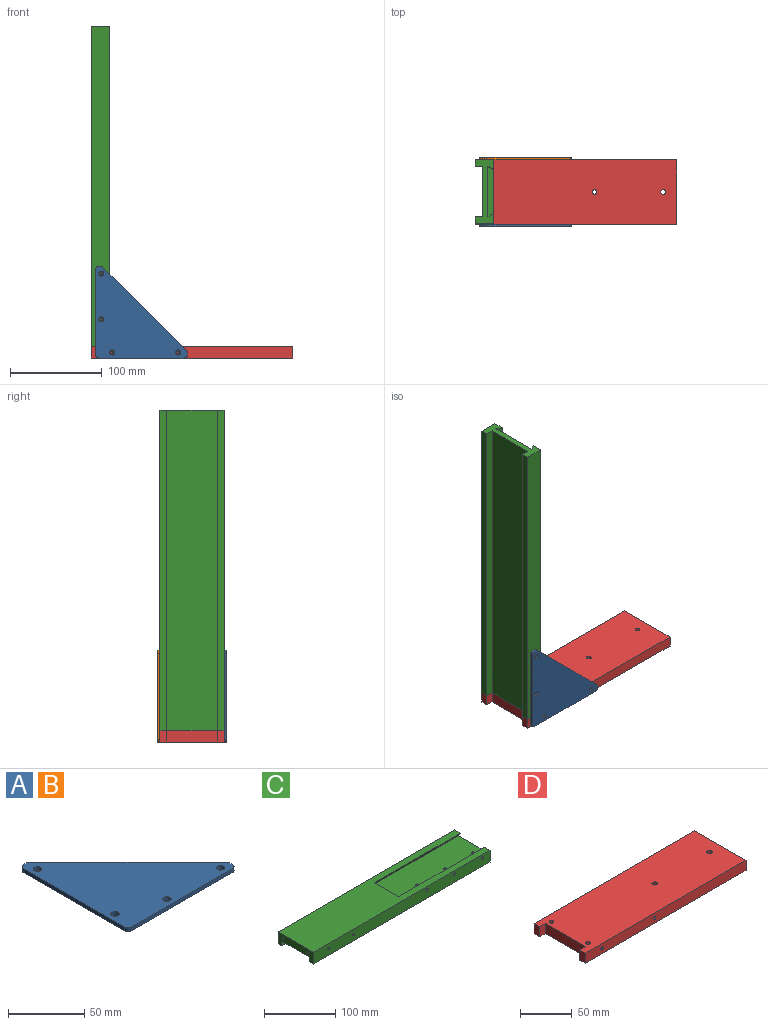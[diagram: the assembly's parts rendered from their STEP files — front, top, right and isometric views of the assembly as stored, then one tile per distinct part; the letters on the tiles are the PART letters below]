
ASSEMBLY  parts=4 mates=3
PART A: 16 faces, bbox 100x100x3 mm
  f0: plane 3x2.76mm, normal (0,1,0), area 8.3mm2, adj f1,f8,f9,f10
  f1: cylinder r=3mm len=3mm, axis (0,0,1), area 14.1mm2, adj f0,f2,f8,f9
  f2: plane 94x3mm, normal (-1,0,0), area 282mm2, adj f1,f3,f8,f9
  f3: cylinder r=3mm len=3mm, axis (0,0,1), area 14.1mm2, adj f2,f4,f8,f9
  f4: plane 94x3mm, normal (0,-1,0), area 282mm2, adj f3,f5,f8,f9
  f5: cylinder r=3mm len=3mm, axis (0,0,1), area 14.1mm2, adj f4,f6,f8,f9
  f6: plane 3x2.76mm, normal (1,0,0), area 8.3mm2, adj f5,f8,f9,f11
  f7: plane 91.24x91.24mm, normal (0.71,0.71,0), area 387.1mm2, adj f8,f9,f10,f11
  f8: plane 100x100mm, normal (0,0,1), area 5574.3mm2, adj f0,f1,f2,f3,f4,f5,f6,f7
  f9: plane 100x100mm, normal (0,0,-1), area 5574.3mm2, adj f0,f1,f2,f3,f4,f5,f6,f7
  f10: cylinder r=3mm len=3mm, axis (0,0,1), area 7.1mm2, adj f0,f7,f8,f9
  f11: cylinder r=3mm len=3mm, axis (0,0,1), area 7.1mm2, adj f6,f7,f8,f9
  f12: cylinder r=2.75mm len=5.5mm, axis (0,0,1), area 51.8mm2, adj f8,f9
  f13: cylinder r=2.75mm len=5.5mm, axis (0,0,1), area 51.8mm2, adj f8,f9
  f14: cylinder r=2.75mm len=5.5mm, axis (0,0,1), area 51.8mm2, adj f8,f9
  f15: cylinder r=2.75mm len=5.5mm, axis (0,0,1), area 51.8mm2, adj f8,f9
PART B: same geometry as A
PART C: 32 faces, bbox 350x70x20 mm
  f0: plane 170x55mm, normal (0,0,1), area 9166.6mm2, adj f2,f8,f24,f25,f26,f27,f28,f29
  f1: plane 350x7.5mm, normal (0,0,-1), area 2625mm2, adj f2,f4,f5,f9
  f2: plane 70x20mm, normal (1,0,0), area 651mm2, adj f0,f1,f3,f4,f6,f7,f9,f10
  f3: plane 350x20mm, normal (0,-1,0), area 6922.6mm2, adj f2,f5,f6,f7,f21,f23,f25,f27
  f4: plane 350x20mm, normal (0,1,0), area 6983.9mm2, adj f1,f2,f5,f6,f17,f19
  f5: plane 70x20mm, normal (-1,0,0), area 943.9mm2, adj f1,f3,f4,f6,f7,f9,f10,f11
  f6: plane 350x70mm, normal (0,0,1), area 16340mm2, adj f2,f3,f4,f5,f8,f30,f31
  f7: plane 350x7.5mm, normal (0,0,-1), area 2625mm2, adj f2,f3,f5,f10
  f8: plane 55x6mm, normal (1,0,0), area 309mm2, adj f0,f6,f30,f31
  f9: plane 350x8mm, normal (0,-1,0), area 2800mm2, adj f1,f2,f5,f11
  f10: plane 350x8mm, normal (0,1,0), area 2800mm2, adj f2,f5,f7,f11
  f11: plane 350x55mm, normal (0,0,-1), area 19250mm2, adj f2,f5,f9,f10
  f12: cone r=0mm half-angle=59deg, axis (-1,0,0), area 9.4mm2, adj f13
  f13: cylinder r=1.6mm len=15mm, axis (-1,0,0), area 150.8mm2, adj f5,f12
  f14: cone r=0mm half-angle=59deg, axis (-1,0,0), area 9.4mm2, adj f15
  f15: cylinder r=1.6mm len=15mm, axis (-1,0,0), area 150.8mm2, adj f5,f14
  f16: cone r=0mm half-angle=59deg, axis (0,1,0), area 9.4mm2, adj f17
  f17: cylinder r=1.6mm len=15mm, axis (0,1,0), area 150.8mm2, adj f4,f16
  f18: cone r=0mm half-angle=59deg, axis (0,1,0), area 9.4mm2, adj f19
  f19: cylinder r=1.6mm len=15mm, axis (0,1,0), area 150.8mm2, adj f4,f18
  f20: cone r=0mm half-angle=59deg, axis (0,-1,0), area 9.4mm2, adj f21
  f21: cylinder r=1.6mm len=15mm, axis (0,-1,0), area 150.8mm2, adj f3,f20
  f22: cone r=0mm half-angle=59deg, axis (0,-1,0), area 9.4mm2, adj f23
  f23: cylinder r=1.6mm len=15mm, axis (0,-1,0), area 150.8mm2, adj f3,f22
  f24: cone r=0mm half-angle=59deg, axis (0,-1,0), area 6.1mm2, adj f0,f25
  f25: cylinder r=2.55mm len=20mm, axis (0,-1,0), area 207.7mm2, adj f0,f3,f24,f30
  f26: cone r=0mm half-angle=59deg, axis (0,-1,0), area 6.1mm2, adj f0,f27
  f27: cylinder r=2.55mm len=20mm, axis (0,-1,0), area 207.7mm2, adj f0,f3,f26,f30
  f28: cone r=0mm half-angle=59deg, axis (0,-1,0), area 6.1mm2, adj f0,f29
  f29: cylinder r=2.55mm len=20mm, axis (0,-1,0), area 207.7mm2, adj f0,f3,f28,f30
  f30: plane 170x6mm, normal (0,0.87,-0.5), area 1125.2mm2, adj f0,f2,f6,f8,f25,f27,f29
  f31: plane 170x6mm, normal (0,-0.86,-0.51), area 1183.9mm2, adj f0,f2,f6,f8
PART D: 26 faces, bbox 220x70x12 mm
  f0: cylinder r=2.25mm len=8mm, axis (0,0,-1), area 113.1mm2, adj f10,f15
  f1: cylinder r=2.25mm len=8mm, axis (0,0,-1), area 113.1mm2, adj f10,f13
  f2: plane 220x12mm, normal (0,-1,0), area 2623.9mm2, adj f3,f9,f10,f11,f23,f25
  f3: plane 70x12mm, normal (1,0,0), area 840mm2, adj f2,f4,f10,f11
  f4: plane 220x12mm, normal (0,1,0), area 2623.9mm2, adj f3,f5,f10,f11,f19,f21
  f5: plane 12x7.5mm, normal (-1,0,0), area 90mm2, adj f4,f6,f10,f11
  f6: plane 12x8mm, normal (0,-1,0), area 96mm2, adj f5,f7,f10,f11
  f7: plane 55x12mm, normal (-1,0,0), area 660mm2, adj f6,f8,f10,f11
  f8: plane 12x8mm, normal (0,1,0), area 96mm2, adj f7,f9,f10,f11
  f9: plane 12x7.5mm, normal (-1,0,0), area 90mm2, adj f2,f8,f10,f11
  f10: plane 220x70mm, normal (0,0,1), area 14887.3mm2, adj f0,f1,f2,f3,f4,f5,f6,f7
  f11: plane 220x70mm, normal (0,0,-1), area 14818.6mm2, adj f2,f3,f4,f5,f6,f7,f8,f9
  f12: cylinder r=4mm len=8mm, axis (0,0,-1), area 100.5mm2, adj f11,f13
  f13: plane 8x8mm, normal (0,0,-1), area 34.4mm2, adj f1,f12
  f14: cylinder r=4mm len=8mm, axis (0,0,-1), area 100.5mm2, adj f11,f15
  f15: plane 8x8mm, normal (0,0,-1), area 34.4mm2, adj f0,f14
  f16: cylinder r=2.55mm len=12mm, axis (0,0,-1), area 192.3mm2, adj f10,f11
  f17: cylinder r=2.55mm len=12mm, axis (0,0,-1), area 192.3mm2, adj f10,f11
  f18: cone r=0mm half-angle=59deg, axis (0,1,0), area 9.4mm2, adj f19
  f19: cylinder r=1.6mm len=15mm, axis (0,1,0), area 150.8mm2, adj f4,f18
  f20: cone r=0mm half-angle=59deg, axis (0,1,0), area 9.4mm2, adj f21
  f21: cylinder r=1.6mm len=15mm, axis (0,1,0), area 150.8mm2, adj f4,f20
  f22: cone r=0mm half-angle=59deg, axis (0,-1,0), area 9.4mm2, adj f23
  f23: cylinder r=1.6mm len=15mm, axis (0,-1,0), area 150.8mm2, adj f2,f22
  f24: cone r=0mm half-angle=59deg, axis (0,-1,0), area 9.4mm2, adj f25
  f25: cylinder r=1.6mm len=15mm, axis (0,-1,0), area 150.8mm2, adj f2,f24
PLACE A rot(axis=(-0.58,-0.58,-0.58),120deg) t=(-75,-38,50)mm
PLACE B rot(axis=(-0.58,-0.58,-0.58),120deg) t=(-75,35,50)mm
PLACE C rot(axis=(0.71,0,0.71),180deg) t=(-130,0,187)mm
PLACE D t=(-20,0,0)mm
MATE fastened C.f14 <-> D.f0  axis (0,0,-1) through (-116,25,12)mm
MATE fastened B.f15 <-> D.f18  axis (0,-1,0) through (-35,35,6)mm
MATE fastened D.f18 <-> A.f15  axis (0,-1,0) through (-35,-35,6)mm
